FCSTD DOCUMENT  (FreeCAD 0.16RUnknown)
Label: srx-follower0
License: All rights reserved
LicenseURL: http://en.wikipedia.org/wiki/All_rights_reserved
objects: Sketcher::SketchObject×1
note: 1 computed .brp shape members not serialized (recipe doc carries the construction recipe); baked Part::Feature solids carry a one-line shape summary decoded from their .brp

FEATURE [Sketcher::SketchObject] Sketch
  sketch-geometry (11):
    g0: LineSegment StartX=8.37066 StartY=17.5299 StartZ=0 EndX=13.3975 EndY=-0.000730048 EndZ=0
    g1: LineSegment StartX=13.3975 StartY=-0.000730048 StartZ=0 EndX=24.5975 EndY=-0.000730048 EndZ=0
    g2: LineSegment StartX=24.5975 StartY=-0.000730048 StartZ=0 EndX=24.5975 EndY=27.9993 EndZ=0
    g3: LineSegment StartX=24.5975 StartY=27.9993 StartZ=0 EndX=4.81566 EndY=35.1993 EndZ=0
    g4: LineSegment StartX=4.81566 StartY=35.1993 StartZ=0 EndX=-0.00250129 EndY=34.3497 EndZ=0
    g5: LineSegment StartX=-0.00250129 StartY=34.3497 StartZ=0 EndX=-0.00250129 EndY=17.5144 EndZ=0
    g6: LineSegment StartX=7.28408 StartY=17.5299 StartZ=0 EndX=7.28408 EndY=3.11441 EndZ=0
    g7: LineSegment StartX=7.28408 StartY=3.11441 StartZ=0 EndX=1.08408 EndY=3.11441 EndZ=0
    g8: LineSegment StartX=1.08408 StartY=3.11441 StartZ=0 EndX=1.08408 EndY=17.5144 EndZ=0
    g9: LineSegment StartX=-0.00250129 StartY=17.5144 StartZ=0 EndX=1.08408 EndY=17.5144 EndZ=0
    g10: LineSegment StartX=7.28408 StartY=17.5299 StartZ=0 EndX=8.37066 EndY=17.5299 EndZ=0
  constraints (30):
    c: Coincident(g0,g1)
    c: Horizontal(g1)
    c: Coincident(g1,g2)
    c: Vertical(g2)
    c: Coincident(g2,g3)
    c: Coincident(g3,g4)
    c: Coincident(g4,g5)
    c: Vertical(g5)
    c: Distance(g2) = 28
    c: Angle(g4,g3) = 2.61799
    c: Angle(g3,g2) = 1.91986
    c: Distance(g1) = 11.2
    c: Coincident(g6,g7)
    c: Coincident(g7,g8)
    c: Horizontal(g7)
    c: Vertical(g6)
    c: Vertical(g8)
    c: Angle(g10,g0) = 1.85005
    c: Equal(g9,g10)
    c: Distance(g7) = 6.2
    c: Coincident(g9,g8)
    c: Coincident(g9,g5)
    c: Coincident(g10,g6)
    c: Coincident(g10,g0)
    c: Horizontal(g9)
    c: Horizontal(g10)
    c: Parallel(g5,g2)
    c: DistanceX(g4,g2) = 24.6
    c: DistanceY(g0,g3) = 35.2
    c: Distance(g8) = 14.4
